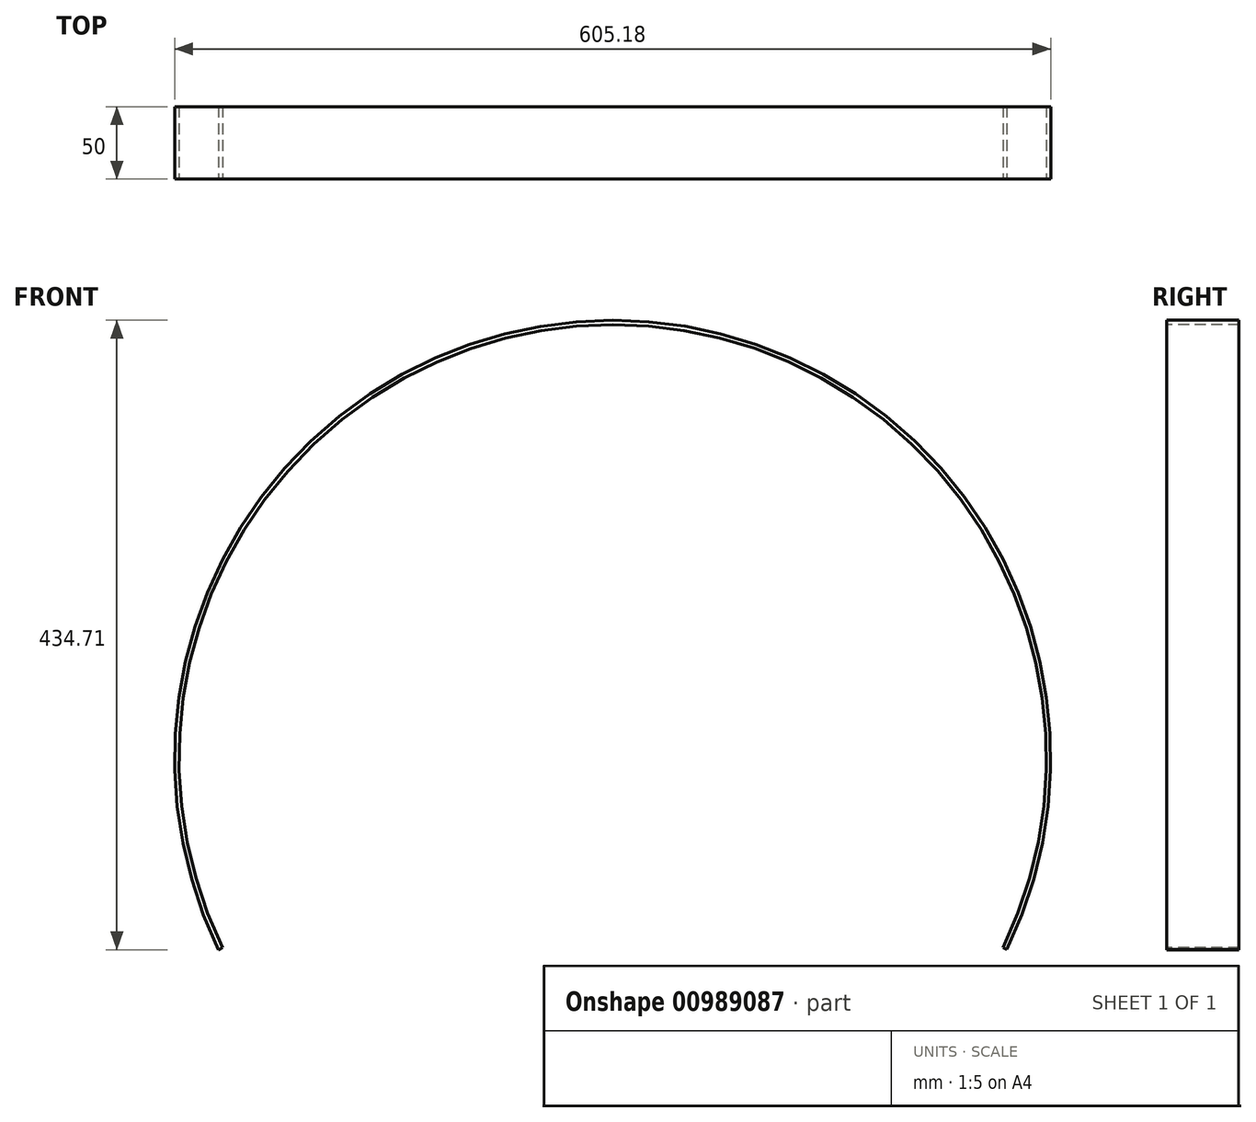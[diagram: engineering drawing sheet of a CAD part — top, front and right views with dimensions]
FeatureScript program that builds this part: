
annotation { "Feature Type Name" : "Feature", "Feature Type Description" : "" }
export const myFeature = defineFeature(function(context is Context, id is Id, definition is map)
    precondition{}
    {
        {
            var Q0;
            Q0=qCreatedBy(makeId("Front.planeOp"),FACE);
            var sketch = newSketch(context, id + "F0", { "sketchPlane" : qUnion([Q0])});
            skArc(sketch, "E0", {"start": v(-269.52, -130.81) * mm, "mid": v(-0.05, 299.59) * mm, "end": v(269.56, -130.72) * mm});
            skArc(sketch, "E1", {"start": v(-272.22, -132.12) * mm, "mid": v(-0.05, 302.59) * mm, "end": v(272.26, -132.03) * mm});
            skLineSegment(sketch, "E2", {"start": v(-272.22, -132.12) * mm, "end": v(-269.52, -130.81) * mm});
            skLineSegment(sketch, "E3", {"start": v(269.56, -130.72) * mm, "end": v(272.26, -132.03) * mm});
            skSolve(sketch);
        }
        {
            var Q0;
            Q0 = qSketchRegion(id + "F0", true);
            extrude(context, id + "F1", {"entities" : qUnion([Q0]), "oppositeDirection" : true, "depth" : 50 * mm, "offsetDistance" : 25 * mm});
        }
    });
